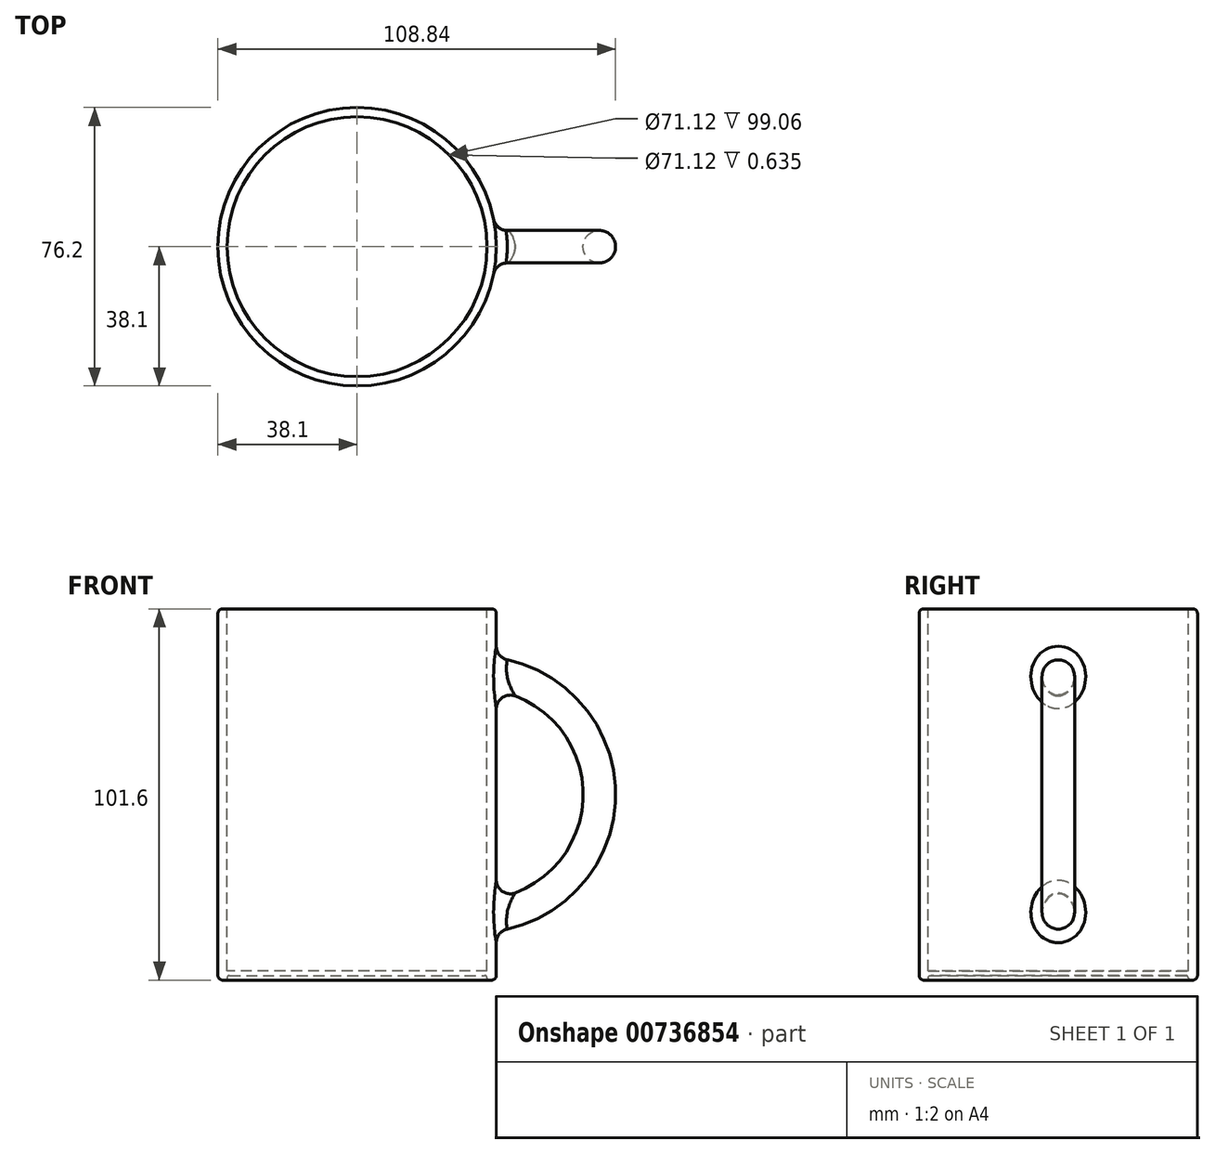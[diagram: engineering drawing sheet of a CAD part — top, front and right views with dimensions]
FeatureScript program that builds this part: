
annotation { "Feature Type Name" : "Feature", "Feature Type Description" : "" }
export const myFeature = defineFeature(function(context is Context, id is Id, definition is map)
    precondition{}
    {
        {
            var Q0;
            Q0=qCreatedBy(makeId("Top.planeOp"),FACE);
            var sketch = newSketch(context, id + "F0", { "sketchPlane" : qUnion([Q0])});
            skCircle(sketch, "E0", {"center": v(0, 0) * mm, "radius": 38.1 * mm});
            skSolve(sketch);
        }
        {
            var Q0;
            Q0 = qSketchRegion(id + "F0", true);
            extrude(context, id + "F1", {"entities" : qUnion([Q0]), "endBound" : BoundingType.SYMMETRIC, "depth" : 101.6 * mm, "offsetDistance" : 25.4 * mm});
        }
        {
            var Q0;
            Q0=makeQuery(id+"F1.opExtrude","CAP_FACE",FACE,{"disambiguationData":[OSD([sQuery(id+"F0.wireOp",EDGE,"E0")])],"isStart":false});
            var sketch = newSketch(context, id + "F2", { "sketchPlane" : qUnion([Q0])});
            skCircle(sketch, "E1", {"center": v(0, 0) * mm, "radius": 35.56 * mm});
            skSolve(sketch);
        }
        {
            var Q0;
            Q0 = qSketchRegion(id + "F2", true);
            extrude(context, id + "F3", {"entities" : qUnion([Q0]), "operationType" : NewBodyOperationType.REMOVE, "oppositeDirection" : true, "depth" : 99.06 * mm, "offsetDistance" : 25.4 * mm});
        }
        {
            var Q0;
            Q0=makeQuery(id+"F1.opExtrude","CAP_EDGE",EDGE,{"disambiguationData":[OSD([sQuery(id+"F0.wireOp",EDGE,"E0")])],"isStart":false});
            var Q1;
            Q1=makeQuery(id+"F3.boolean.opBoolean","COPY",EDGE,{"derivedFrom":makeQuery(id+"F3.opExtrude","CAP_EDGE",EDGE,{"disambiguationData":[OSD([sQuery(id+"F2.wireOp",EDGE,"E1")])],"isStart":true})});
            fillet(context, id + "F4", {"entities" : qUnion([Q0, Q1]), "radius" : 1.27 * mm, "tangentPropagation" : true, "allowEdgeOverflow" : false});
        }
        {
            var Q0;
            Q0=makeQuery(id+"F1.opExtrude","CAP_FACE",FACE,{"disambiguationData":[OSD([sQuery(id+"F0.wireOp",EDGE,"E0")])],"isStart":true});
            var sketch = newSketch(context, id + "F5", { "sketchPlane" : qUnion([Q0])});
            skCircle(sketch, "E2", {"center": v(0, 0) * mm, "radius": 35.56 * mm});
            skSolve(sketch);
        }
        {
            var Q0;
            Q0 = qSketchRegion(id + "F5", true);
            extrude(context, id + "F6", {"entities" : qUnion([Q0]), "operationType" : NewBodyOperationType.REMOVE, "oppositeDirection" : true, "depth" : 1.27 * mm, "offsetDistance" : 25.4 * mm});
        }
        {
            var Q0;
            Q0=makeQuery(id+"F6.boolean.opBoolean","COPY",EDGE,{"derivedFrom":makeQuery(id+"F6.opExtrude","CAP_EDGE",EDGE,{"disambiguationData":[OSD([sQuery(id+"F5.wireOp",EDGE,"E2")])],"isStart":true})});
            var Q1;
            Q1=makeQuery(id+"F1.opExtrude","CAP_EDGE",EDGE,{"disambiguationData":[OSD([sQuery(id+"F0.wireOp",EDGE,"E0")])],"isStart":true});
            fillet(context, id + "F7", {"entities" : qUnion([Q0, Q1]), "radius" : 1.27 * mm, "tangentPropagation" : true, "allowEdgeOverflow" : false});
        }
        {
            var Q0;
            Q0=makeQuery(id+"F6.boolean.opBoolean","COPY",FACE,{"derivedFrom":makeQuery(id+"F6.opExtrude","CAP_FACE",FACE,{"disambiguationData":[OSD([sQuery(id+"F5.wireOp",EDGE,"E2")])],"isStart":false})});
            fillet(context, id + "F8", {"entities" : qUnion([Q0]), "radius" : 0.64 * mm, "tangentPropagation" : true, "allowEdgeOverflow" : false});
        }
        {
            var Q0;
            Q0=makeQuery(id+"F3.boolean.opBoolean","COPY",EDGE,{"derivedFrom":makeQuery(id+"F3.opExtrude","CAP_EDGE",EDGE,{"disambiguationData":[OSD([sQuery(id+"F2.wireOp",EDGE,"E1")])],"isStart":false})});
            fillet(context, id + "F9", {"entities" : qUnion([Q0]), "radius" : 1.27 * mm, "tangentPropagation" : true, "allowEdgeOverflow" : false});
        }
        {
            var Q0;
            Q0=qCreatedBy(makeId("Right.planeOp"),FACE);
            cPlane(context, id + "F10", {"entities" : qUnion([Q0]), "cplaneType" : CPlaneType.OFFSET, "offset" : 33.02 * mm, "width" : 152.4 * mm, "height" : 152.4 * mm});
        }
        {
            var Q0;
            Q0=qCreatedBy(id+"F10.planeOp",FACE);
            var sketch = newSketch(context, id + "F11", { "sketchPlane" : qUnion([Q0])});
            skCircle(sketch, "E3", {"center": v(0, -33.27) * mm, "radius": 4.45 * mm});
            skCircle(sketch, "E4.MirrorC", {"center": v(0, 33.27) * mm, "radius": 4.45 * mm});
            skSolve(sketch);
        }
        {
            var Q0;
            Q0=qCreatedBy(makeId("Front.planeOp"),FACE);
            var sketch = newSketch(context, id + "F12", { "sketchPlane" : qUnion([Q0])});
            skPoint(sketch, "E5", {"position": v(33.02, 0) * mm});
            skArc(sketch, "E6", {"start": v(33.02, -33.27) * mm, "mid": v(66.3, 0) * mm, "end": v(33.02, 33.27) * mm});
            skSolve(sketch);
        }
        {
            var Q0;
            Q0 = qSketchRegion(id + "F11", true);
            var Q1;
            Q1 = qConstructionFilter(qBodyType(qCreatedBy(id + "F12" ,EDGE), BodyType.WIRE), ConstructionObject.NO);
            sweep(context, id + "F13", {"operationType" : NewBodyOperationType.ADD, "profiles" : qUnion([Q0]), "path" : qUnion([Q1])});
        }
        {
            var Q0;
            Q0=makeQuery(id+"F13.boolean.opBoolean","INTERSECT",EDGE,{"disambiguationData":[OD(1.0)],"derivedFrom":[makeQuery(id+"F1.opExtrude","SWEPT_FACE",FACE,{"disambiguationData":[OSD([sQuery(id+"F0.wireOp",EDGE,"E0")])]}),makeQuery(id+"F13.opSweep","SWEPT_FACE",FACE,{"disambiguationData":[OSD([sQuery(id+"F11.wireOp",EDGE,"E3"),sQuery(id+"F12.wireOp",EDGE,"E6")])]})]});
            var Q1;
            Q1=makeQuery(id+"F13.boolean.opBoolean","INTERSECT",EDGE,{"disambiguationData":[OD(0.0)],"derivedFrom":[makeQuery(id+"F1.opExtrude","SWEPT_FACE",FACE,{"disambiguationData":[OSD([sQuery(id+"F0.wireOp",EDGE,"E0")])]}),makeQuery(id+"F13.opSweep","SWEPT_FACE",FACE,{"disambiguationData":[OSD([sQuery(id+"F11.wireOp",EDGE,"E3"),sQuery(id+"F12.wireOp",EDGE,"E6")])]})]});
            fillet(context, id + "F14", {"entities" : qUnion([Q0, Q1]), "radius" : 3.8 * mm, "tangentPropagation" : true, "allowEdgeOverflow" : false});
        }
        {
            var Q0;
            Q0=makeQuery(id+"F3.boolean.opBoolean","COPY",FACE,{"derivedFrom":makeQuery(id+"F3.opExtrude","CAP_FACE",FACE,{"disambiguationData":[OSD([sQuery(id+"F2.wireOp",EDGE,"E1")])],"isStart":false})});
            var sketch = newSketch(context, id + "F15", { "sketchPlane" : qUnion([Q0])});
            skCircle(sketch, "E7", {"center": v(0, 0) * mm, "radius": 35.56 * mm});
            skSolve(sketch);
        }
        {
            var Q0;
            Q0 = qSketchRegion(id + "F15", true);
            extrude(context, id + "F16", {"entities" : qUnion([Q0]), "operationType" : NewBodyOperationType.REMOVE, "depth" : 635 * mm, "offsetDistance" : 25.4 * mm});
        }
    });
